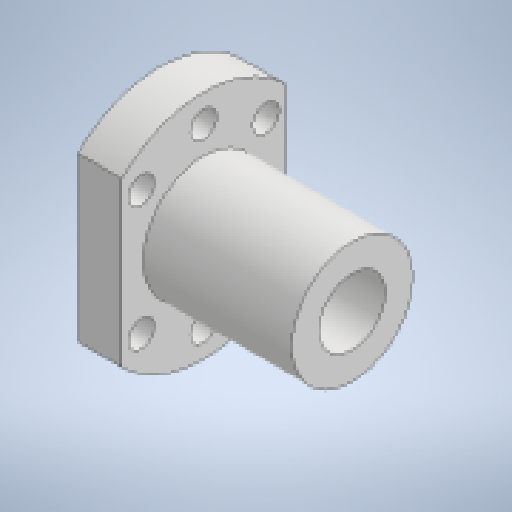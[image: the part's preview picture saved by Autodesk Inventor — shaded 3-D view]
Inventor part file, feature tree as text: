
AUTODESK INVENTOR PART (.ipt)
format: ipt  version: 2023 (Build 270158000, 158)  size: 175,104 bytes
history: native  units: mm
features: sketch x2, revolve x1, extrude x1
ambient origin geometry x8: Origin, YZ Plane, XZ Plane, XY Plane, X Axis, Y Axis, Z Axis, Center Point
bodies: Solid1 (feature_tree)
feature tree (4):
  revolve  "Revolution1"  [1 undecoded]
  extrude  "Extrusion1"  Depth=35.0mm
  sketch  "Sketch1"  dims[d0=11.0mm d1=21.0mm]
  sketch  "Sketch2"  dims[d2=8.0mm d3=35.0mm d4=6.0mm d5=90.0deg d6=45.0deg d7=32.0mm d8=4.8mm d10=10.0mm d11=0.0mm]
note: 1 required parameter value undecoded (feature->parameter linkage not recoverable at this tier; creation-order binding heuristic only, values carry confidence <= 0.55)
